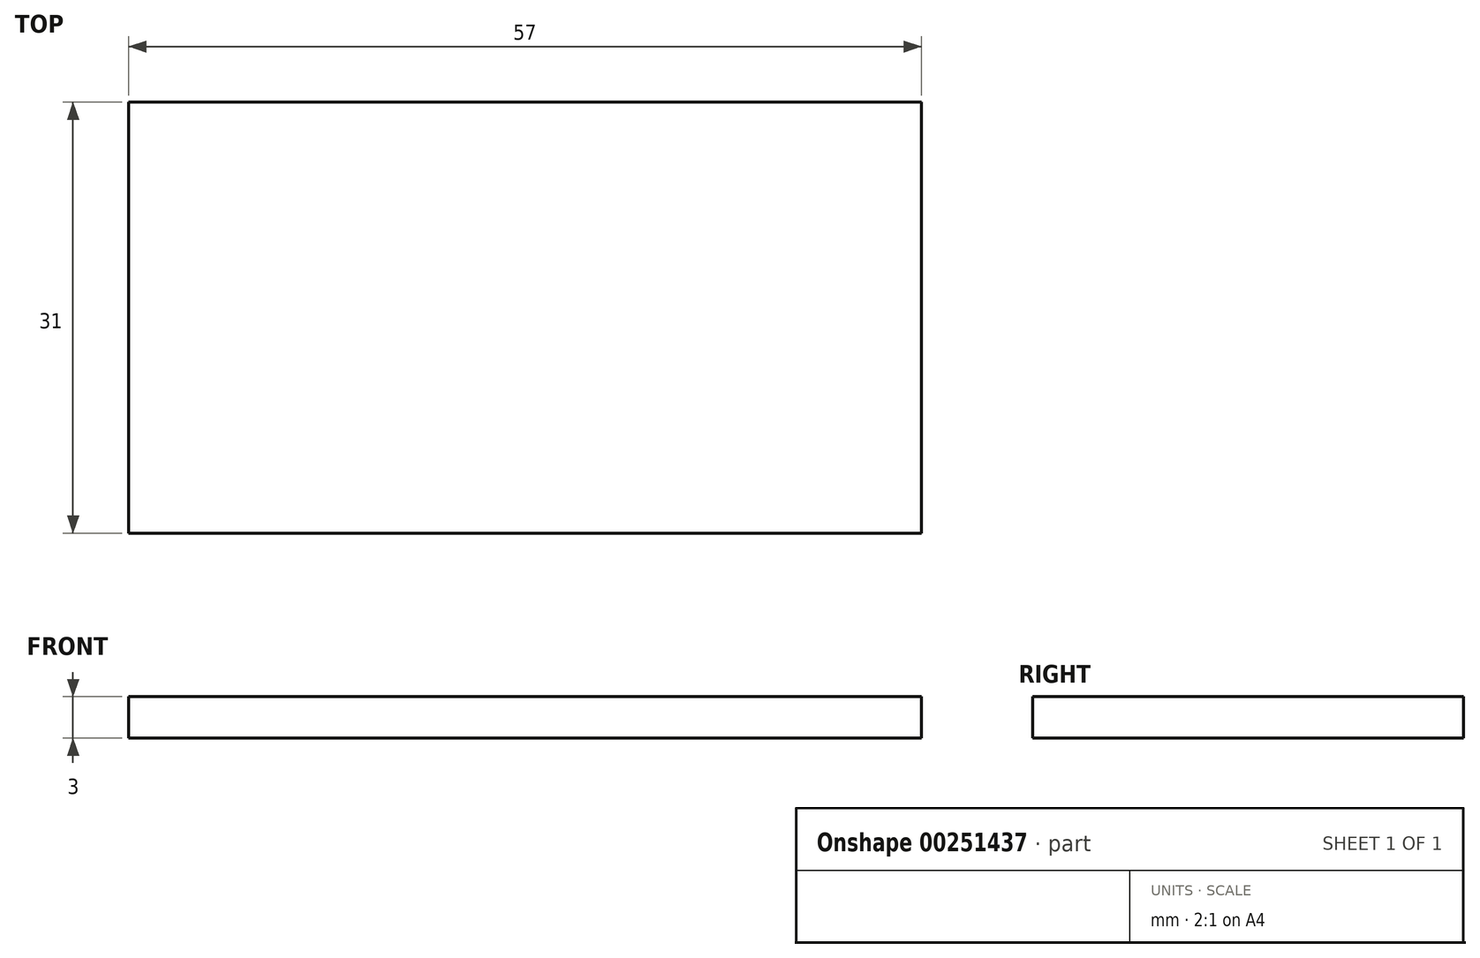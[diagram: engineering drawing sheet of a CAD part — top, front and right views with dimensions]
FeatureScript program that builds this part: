
annotation { "Feature Type Name" : "Feature", "Feature Type Description" : "" }
export const myFeature = defineFeature(function(context is Context, id is Id, definition is map)
    precondition{}
    {
        {
            var Q0;
            Q0=qCreatedBy(makeId("Top.planeOp"),FACE);
            var sketch = newSketch(context, id + "F0", { "sketchPlane" : qUnion([Q0])});
            skLineSegment(sketch, "E0.bottom", {"start": v(28.5, 15.5) * mm, "end": v(-28.5, 15.5) * mm});
            skLineSegment(sketch, "E0.top", {"start": v(28.5, -15.5) * mm, "end": v(-28.5, -15.5) * mm});
            skLineSegment(sketch, "E0.left", {"start": v(28.5, 15.5) * mm, "end": v(28.5, -15.5) * mm});
            skLineSegment(sketch, "E0.right", {"start": v(-28.5, 15.5) * mm, "end": v(-28.5, -15.5) * mm});
            skPoint(sketch, "E0.middle", {"position": v(0, 0) * mm});
            skSolve(sketch);
        }
        {
            var Q0;
            Q0=makeQuery(id+"F0.imprint","IMPRINT",FACE,{"disambiguationData":[TD([[makeQuery(id+"F0.imprint","IMPRINT",EDGE,{"derivedFrom":sQuery(id+"F0.wireOp",EDGE,"E0.bottom")}),1.0]])]});
            extrude(context, id + "F1", {"entities" : qUnion([Q0]), "depth" : 3 * mm});
        }
    });
